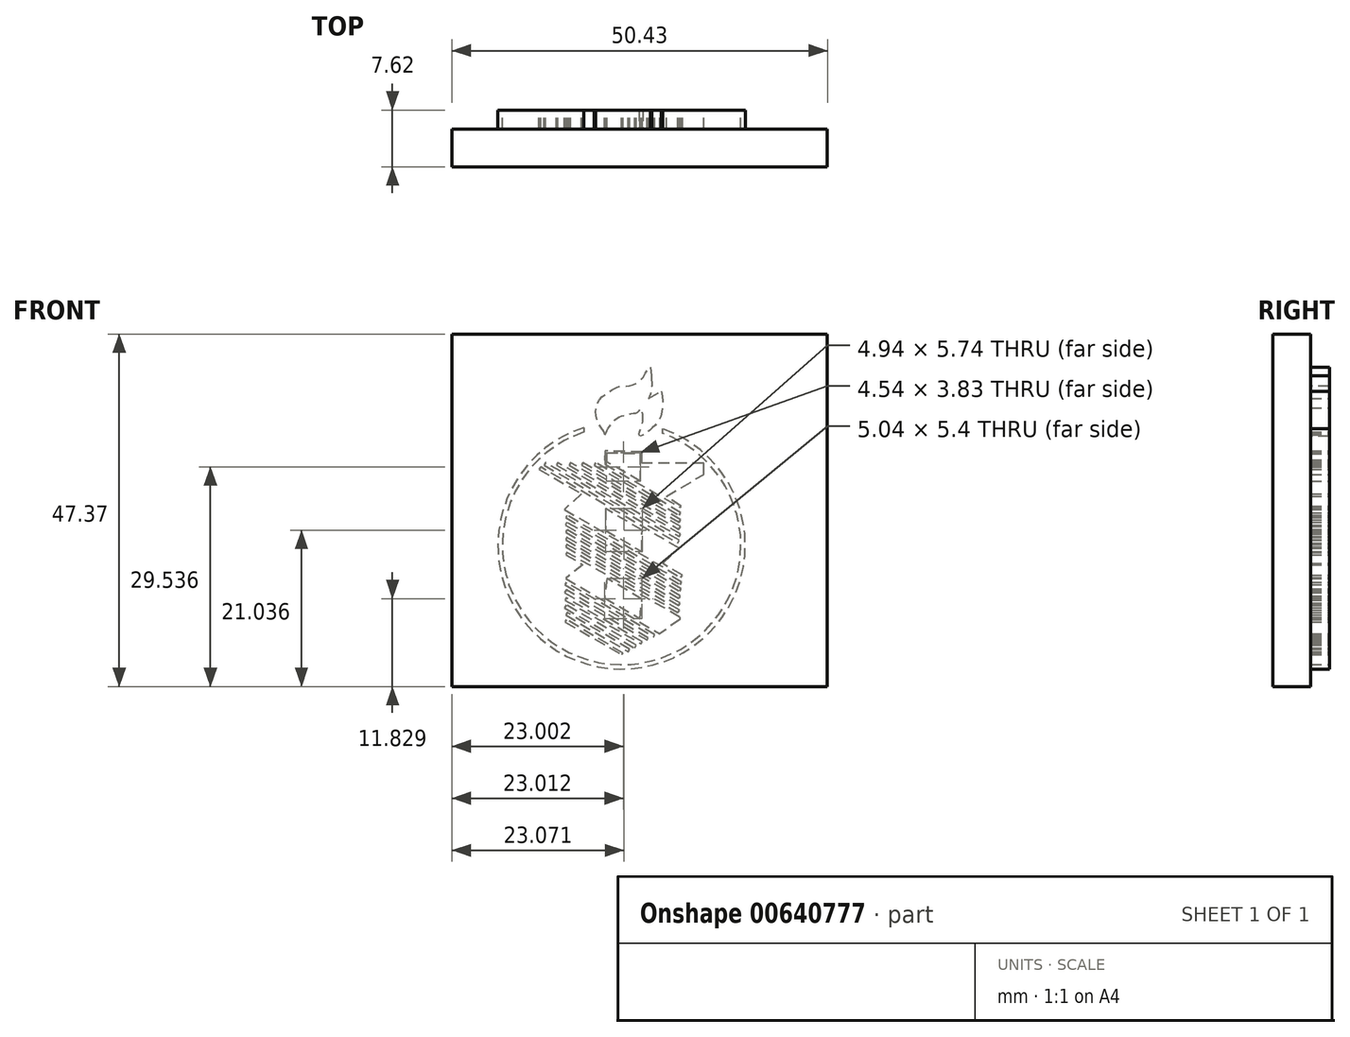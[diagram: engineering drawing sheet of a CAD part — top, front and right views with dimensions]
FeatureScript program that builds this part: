
annotation { "Feature Type Name" : "Feature", "Feature Type Description" : "" }
export const myFeature = defineFeature(function(context is Context, id is Id, definition is map)
    precondition{}
    {
        {
            var Q0;
            Q0=qCreatedBy(makeId("Front.planeOp"),FACE);
            var sketch = newSketch(context, id + "F0", { "sketchPlane" : qUnion([Q0])});
            skArc(sketch, "E0", {"start": v(20.24, 37.87) * mm, "mid": v(25.08, 5.42) * mm, "end": v(30.76, 37.74) * mm});
            skPoint(sketch, "E0.first.point", {"position": v(8.97, 25.16) * mm});
            skPoint(sketch, "E0.second.point", {"position": v(41.48, 18.25) * mm});
            skPoint(sketch, "E0.third.point", {"position": v(33.4, 7.53) * mm});
            skArc(sketch, "E1", {"start": v(20.24, 37.25) * mm, "mid": v(25.08, 6.01) * mm, "end": v(30.76, 37.1) * mm});
            skLineSegment(sketch, "E2", {"start": v(20.24, 37.87) * mm, "end": v(20.24, 37.25) * mm});
            skLineSegment(sketch, "E3", {"start": v(30.76, 37.74) * mm, "end": v(30.76, 37.1) * mm});
            skFitSpline(sketch, "E4", {"points": [v(23.05, 36.92) * mm, v(22.85, 37.48) * mm, v(22.4, 38.11) * mm, v(22.01, 38.86) * mm, v(21.84, 39.64) * mm, v(21.84, 40.27) * mm, v(22.01, 41.04) * mm, v(22.37, 41.63) * mm, v(23.03, 42.32) * mm, v(24.3, 43.12) * mm, v(25.07, 43.44) * mm, v(26.14, 43.44) * mm, v(26.56, 43.54) * mm, v(27.31, 43.8) * mm, v(27.76, 44.12) * mm, v(28.38, 44.9) * mm, v(28.59, 45.41) * mm, v(29.15, 45.99) * mm], "startDerivative": vector(-3, 11.07) * mm, "endDerivative": vector(11.27, 9.68) * mm});
            skLineSegment(sketch, "E5", {"start": v(29.15, 45.99) * mm, "end": v(29.29, 44.84) * mm});
            skFitSpline(sketch, "E6", {"points": [v(29.29, 44.84) * mm, v(29.29, 42.93) * mm, v(28.94, 41.79) * mm], "startDerivative": vector(0.22, -3.65) * mm, "endDerivative": vector(-0.97, -2.41) * mm});
            skLineSegment(sketch, "E7", {"start": v(28.94, 41.79) * mm, "end": v(30.64, 42.74) * mm});
            skFitSpline(sketch, "E8", {"points": [v(30.64, 42.74) * mm, v(30.76, 42.12) * mm, v(30.64, 39.59) * mm, v(29.99, 38.42) * mm, v(28.96, 37.4) * mm, v(27.79, 36.72) * mm, v(27.64, 37.04) * mm, v(28.01, 38.09) * mm, v(28.16, 39.45) * mm, v(28.05, 40.5) * mm], "startDerivative": vector(1.51, -5.83) * mm, "endDerivative": vector(-1.38, 9.53) * mm});
            skFitSpline(sketch, "E9", {"points": [v(23.05, 36.92) * mm, v(23.38, 37.55) * mm, v(23.8, 38.2) * mm, v(24.3, 38.82) * mm, v(24.9, 39.27) * mm, v(25.84, 39.58) * mm, v(26.67, 39.77) * mm, v(27.3, 39.86) * mm, v(27.41, 39.94) * mm, v(27.58, 40.05) * mm, v(27.7, 40.2) * mm, v(28.05, 40.5) * mm], "startDerivative": vector(2.94, 6.1) * mm, "endDerivative": vector(5.03, 3.75) * mm});
            skLineSegment(sketch, "E10", {"start": v(23.26, 33.53) * mm, "end": v(23.26, 34.5) * mm});
            skLineSegment(sketch, "E11", {"start": v(23.26, 34.5) * mm, "end": v(27.8, 34.37) * mm});
            skLineSegment(sketch, "E12", {"start": v(27.8, 34.37) * mm, "end": v(27.8, 30.68) * mm});
            skLineSegment(sketch, "E13", {"start": v(27.8, 30.68) * mm, "end": v(23.26, 33.28) * mm});
            skLineSegment(sketch, "E14", {"start": v(23.05, 33.28) * mm, "end": v(23.05, 32.94) * mm});
            skLineSegment(sketch, "E15", {"start": v(23.05, 32.94) * mm, "end": v(33.19, 27.13) * mm});
            skLineSegment(sketch, "E16", {"start": v(33.19, 27.13) * mm, "end": v(33.3, 27.34) * mm});
            skLineSegment(sketch, "E17", {"start": v(33.3, 27.34) * mm, "end": v(31.33, 28.64) * mm});
            skLineSegment(sketch, "E18", {"start": v(31.33, 28.64) * mm, "end": v(36.34, 31.59) * mm});
            skLineSegment(sketch, "E19", {"start": v(36.34, 31.59) * mm, "end": v(36.34, 33.07) * mm});
            skLineSegment(sketch, "E20", {"start": v(36.34, 33.07) * mm, "end": v(28.05, 33.07) * mm});
            skLineSegment(sketch, "E21", {"start": v(28.05, 33.07) * mm, "end": v(28.05, 34.59) * mm});
            skLineSegment(sketch, "E22", {"start": v(28.05, 34.59) * mm, "end": v(23.05, 34.74) * mm});
            skLineSegment(sketch, "E23", {"start": v(23.05, 34.74) * mm, "end": v(23.02, 33.53) * mm});
            skLineSegment(sketch, "E24", {"start": v(21.8, 33.17) * mm, "end": v(21.62, 32.86) * mm});
            skLineSegment(sketch, "E25", {"start": v(21.62, 32.86) * mm, "end": v(33.06, 26.1) * mm});
            skLineSegment(sketch, "E26", {"start": v(33.06, 26.1) * mm, "end": v(33.26, 26.44) * mm});
            skLineSegment(sketch, "E27", {"start": v(33.26, 26.44) * mm, "end": v(21.8, 33.17) * mm});
            skLineSegment(sketch, "E28", {"start": v(20.1, 33.17) * mm, "end": v(19.9, 32.83) * mm});
            skLineSegment(sketch, "E29", {"start": v(19.9, 32.83) * mm, "end": v(33.02, 25.13) * mm});
            skLineSegment(sketch, "E30", {"start": v(33.02, 25.13) * mm, "end": v(33.23, 25.49) * mm});
            skLineSegment(sketch, "E31", {"start": v(33.23, 25.49) * mm, "end": v(20.1, 33.17) * mm});
            skLineSegment(sketch, "E32", {"start": v(18.44, 33.17) * mm, "end": v(18.24, 32.83) * mm});
            skLineSegment(sketch, "E33", {"start": v(18.24, 32.83) * mm, "end": v(32.98, 24.18) * mm});
            skLineSegment(sketch, "E34", {"start": v(32.98, 24.18) * mm, "end": v(33.21, 24.58) * mm});
            skLineSegment(sketch, "E35", {"start": v(33.21, 24.58) * mm, "end": v(18.44, 33.17) * mm});
            skLineSegment(sketch, "E36", {"start": v(16.75, 33.17) * mm, "end": v(16.55, 32.83) * mm});
            skLineSegment(sketch, "E37", {"start": v(16.55, 32.83) * mm, "end": v(33.02, 23.25) * mm});
            skLineSegment(sketch, "E38", {"start": v(33.02, 23.25) * mm, "end": v(33.21, 23.58) * mm});
            skLineSegment(sketch, "E39", {"start": v(33.21, 23.58) * mm, "end": v(16.75, 33.17) * mm});
            skLineSegment(sketch, "E40", {"start": v(15.08, 33.17) * mm, "end": v(14.88, 32.83) * mm});
            skLineSegment(sketch, "E41", {"start": v(14.88, 32.83) * mm, "end": v(32.84, 22.38) * mm});
            skLineSegment(sketch, "E42", {"start": v(32.84, 22.38) * mm, "end": v(33.02, 22.7) * mm});
            skLineSegment(sketch, "E43", {"start": v(33.02, 22.7) * mm, "end": v(15.08, 33.17) * mm});
            skLineSegment(sketch, "E44", {"start": v(14.41, 32.58) * mm, "end": v(14.21, 32.23) * mm});
            skLineSegment(sketch, "E45", {"start": v(14.21, 32.23) * mm, "end": v(19.9, 28.97) * mm});
            skLineSegment(sketch, "E46", {"start": v(19.9, 28.97) * mm, "end": v(17.61, 26.89) * mm});
            skLineSegment(sketch, "E47", {"start": v(17.61, 26.89) * mm, "end": v(33.24, 17.72) * mm});
            skLineSegment(sketch, "E48", {"start": v(33.24, 17.72) * mm, "end": v(33.47, 18.05) * mm});
            skLineSegment(sketch, "E49", {"start": v(33.47, 18.05) * mm, "end": v(30.81, 19.6) * mm});
            skLineSegment(sketch, "E50", {"start": v(30.81, 19.6) * mm, "end": v(33.02, 21.67) * mm});
            skLineSegment(sketch, "E51", {"start": v(33.02, 21.67) * mm, "end": v(14.41, 32.58) * mm});
            skLineSegment(sketch, "E52", {"start": v(17.96, 26.06) * mm, "end": v(17.79, 25.77) * mm});
            skLineSegment(sketch, "E53", {"start": v(17.79, 25.77) * mm, "end": v(33.18, 16.76) * mm});
            skLineSegment(sketch, "E54", {"start": v(33.18, 16.76) * mm, "end": v(33.37, 17.1) * mm});
            skLineSegment(sketch, "E55", {"start": v(33.37, 17.1) * mm, "end": v(17.96, 26.06) * mm});
            skLineSegment(sketch, "E56", {"start": v(17.96, 25.13) * mm, "end": v(17.76, 24.79) * mm});
            skLineSegment(sketch, "E57", {"start": v(17.76, 24.79) * mm, "end": v(33.13, 15.86) * mm});
            skLineSegment(sketch, "E58", {"start": v(33.13, 15.86) * mm, "end": v(33.32, 16.18) * mm});
            skLineSegment(sketch, "E59", {"start": v(33.32, 16.18) * mm, "end": v(17.96, 25.13) * mm});
            skLineSegment(sketch, "E60", {"start": v(17.96, 24.13) * mm, "end": v(17.78, 23.81) * mm});
            skLineSegment(sketch, "E61", {"start": v(17.78, 23.81) * mm, "end": v(33.02, 14.93) * mm});
            skLineSegment(sketch, "E62", {"start": v(33.02, 14.93) * mm, "end": v(33.2, 15.23) * mm});
            skLineSegment(sketch, "E63", {"start": v(33.2, 15.23) * mm, "end": v(17.96, 24.13) * mm});
            skLineSegment(sketch, "E64", {"start": v(17.96, 23.12) * mm, "end": v(17.78, 22.81) * mm});
            skLineSegment(sketch, "E65", {"start": v(17.78, 22.81) * mm, "end": v(32.95, 14) * mm});
            skLineSegment(sketch, "E66", {"start": v(32.95, 14) * mm, "end": v(33.15, 14.28) * mm});
            skLineSegment(sketch, "E67", {"start": v(33.15, 14.28) * mm, "end": v(17.96, 23.12) * mm});
            skLineSegment(sketch, "E68", {"start": v(17.96, 22.17) * mm, "end": v(17.78, 21.86) * mm});
            skLineSegment(sketch, "E69", {"start": v(17.78, 21.86) * mm, "end": v(32.86, 13.03) * mm});
            skLineSegment(sketch, "E70", {"start": v(32.86, 13.03) * mm, "end": v(33.08, 13.33) * mm});
            skLineSegment(sketch, "E71", {"start": v(33.08, 13.33) * mm, "end": v(17.96, 22.17) * mm});
            skLineSegment(sketch, "E72", {"start": v(17.96, 21.1) * mm, "end": v(17.78, 20.8) * mm});
            skLineSegment(sketch, "E73", {"start": v(17.78, 20.8) * mm, "end": v(20.1, 19.46) * mm});
            skLineSegment(sketch, "E74", {"start": v(20.1, 19.46) * mm, "end": v(17.78, 17.58) * mm});
            skLineSegment(sketch, "E75", {"start": v(17.78, 17.58) * mm, "end": v(30.44, 10.17) * mm});
            skLineSegment(sketch, "E76", {"start": v(33.12, 12.42) * mm, "end": v(17.96, 21.1) * mm});
            skLineSegment(sketch, "E77", {"start": v(23.14, 26.97) * mm, "end": v(23.12, 24.05) * mm});
            skLineSegment(sketch, "E78", {"start": v(23.12, 24.05) * mm, "end": v(28, 21.23) * mm});
            skLineSegment(sketch, "E79", {"start": v(28, 21.23) * mm, "end": v(28.06, 24.08) * mm});
            skLineSegment(sketch, "E80", {"start": v(28.06, 24.08) * mm, "end": v(23.14, 26.97) * mm});
            skLineSegment(sketch, "E81", {"start": v(23.3, 17.6) * mm, "end": v(23, 15) * mm});
            skLineSegment(sketch, "E82", {"start": v(23, 15) * mm, "end": v(27.78, 12.19) * mm});
            skLineSegment(sketch, "E83", {"start": v(27.78, 12.19) * mm, "end": v(28.04, 14.82) * mm});
            skLineSegment(sketch, "E84", {"start": v(28.04, 14.82) * mm, "end": v(23.3, 17.6) * mm});
            skLineSegment(sketch, "E85", {"start": v(17.84, 17.1) * mm, "end": v(17.65, 16.77) * mm});
            skLineSegment(sketch, "E86", {"start": v(17.65, 16.77) * mm, "end": v(29.61, 9.77) * mm});
            skLineSegment(sketch, "E87", {"start": v(29.61, 9.77) * mm, "end": v(29.77, 10.04) * mm});
            skLineSegment(sketch, "E88", {"start": v(29.77, 10.04) * mm, "end": v(17.84, 17.1) * mm});
            skLineSegment(sketch, "E89", {"start": v(17.84, 16.05) * mm, "end": v(17.63, 15.68) * mm});
            skLineSegment(sketch, "E90", {"start": v(17.63, 15.68) * mm, "end": v(28.72, 9.33) * mm});
            skLineSegment(sketch, "E91", {"start": v(28.72, 9.33) * mm, "end": v(28.87, 9.6) * mm});
            skLineSegment(sketch, "E92", {"start": v(28.87, 9.6) * mm, "end": v(17.84, 16.05) * mm});
            skLineSegment(sketch, "E93", {"start": v(17.84, 15) * mm, "end": v(17.66, 14.7) * mm});
            skLineSegment(sketch, "E94", {"start": v(17.66, 14.7) * mm, "end": v(27.92, 8.82) * mm});
            skLineSegment(sketch, "E95", {"start": v(27.92, 8.82) * mm, "end": v(28.06, 9.06) * mm});
            skLineSegment(sketch, "E96", {"start": v(28.06, 9.06) * mm, "end": v(17.84, 15) * mm});
            skLineSegment(sketch, "E97", {"start": v(17.84, 14.05) * mm, "end": v(17.61, 13.65) * mm});
            skLineSegment(sketch, "E98", {"start": v(17.61, 13.65) * mm, "end": v(27.04, 8.25) * mm});
            skLineSegment(sketch, "E99", {"start": v(27.04, 8.25) * mm, "end": v(27.26, 8.62) * mm});
            skLineSegment(sketch, "E100", {"start": v(27.26, 8.62) * mm, "end": v(17.84, 14.05) * mm});
            skLineSegment(sketch, "E101", {"start": v(17.97, 13.02) * mm, "end": v(17.78, 12.68) * mm});
            skLineSegment(sketch, "E102", {"start": v(17.78, 12.68) * mm, "end": v(26.2, 7.74) * mm});
            skLineSegment(sketch, "E103", {"start": v(26.2, 7.74) * mm, "end": v(26.39, 8.08) * mm});
            skLineSegment(sketch, "E104", {"start": v(26.39, 8.08) * mm, "end": v(17.97, 13.02) * mm});
            skLineSegment(sketch, "E105", {"start": v(17.88, 12.07) * mm, "end": v(17.69, 11.72) * mm});
            skLineSegment(sketch, "E106", {"start": v(17.69, 11.72) * mm, "end": v(25.28, 7.38) * mm});
            skLineSegment(sketch, "E107", {"start": v(25.28, 7.38) * mm, "end": v(25.47, 7.58) * mm});
            skLineSegment(sketch, "E108", {"start": v(25.47, 7.58) * mm, "end": v(17.88, 12.07) * mm});
            skLineSegment(sketch, "E109", {"start": v(33.12, 12.42) * mm, "end": v(33.12, 12.09) * mm});
            skLineSegment(sketch, "E110", {"start": v(33.12, 12.09) * mm, "end": v(30.44, 10.17) * mm});
            skLineSegment(sketch, "E111", {"start": v(23.02, 33.53) * mm, "end": v(23.05, 33.28) * mm});
            skLineSegment(sketch, "E112", {"start": v(23.26, 33.53) * mm, "end": v(23.26, 33.28) * mm});
            skSolve(sketch);
        }
        {
            var Q0;
            Q0=makeQuery(id+"F0.imprint","IMPRINT",FACE,{"disambiguationData":[TD([[makeQuery(id+"F0.imprint","IMPRINT",EDGE,{"derivedFrom":sQuery(id+"F0.wireOp",EDGE,"E0")}),1.0]])]});
            var Q1;
            Q1=makeQuery(id+"F0.imprint","IMPRINT",FACE,{"disambiguationData":[TD([[makeQuery(id+"F0.imprint","IMPRINT",EDGE,{"derivedFrom":sQuery(id+"F0.wireOp",EDGE,"E4")}),-1.0]])]});
            var Q2;
            Q2=makeQuery(id+"F0.imprint","IMPRINT",FACE,{"disambiguationData":[TD([[makeQuery(id+"F0.imprint","IMPRINT",EDGE,{"derivedFrom":sQuery(id+"F0.wireOp",EDGE,"y2vc7ffB-SEBn-57zv-CqBY-3sHhlxAjugWr")}),1.0]])]});
            var Q3;
            Q3=makeQuery(id+"F0.imprint","IMPRINT",FACE,{"disambiguationData":[TD([[makeQuery(id+"F0.imprint","IMPRINT",EDGE,{"derivedFrom":sQuery(id+"F0.wireOp",EDGE,"E24")}),1.0]])]});
            var Q4;
            Q4=makeQuery(id+"F0.imprint","IMPRINT",FACE,{"disambiguationData":[TD([[makeQuery(id+"F0.imprint","IMPRINT",EDGE,{"derivedFrom":sQuery(id+"F0.wireOp",EDGE,"E28")}),1.0]])]});
            var Q5;
            Q5=makeQuery(id+"F0.imprint","IMPRINT",FACE,{"disambiguationData":[TD([[makeQuery(id+"F0.imprint","IMPRINT",EDGE,{"derivedFrom":sQuery(id+"F0.wireOp",EDGE,"E32")}),1.0]])]});
            var Q6;
            Q6=makeQuery(id+"F0.imprint","IMPRINT",FACE,{"disambiguationData":[TD([[makeQuery(id+"F0.imprint","IMPRINT",EDGE,{"derivedFrom":sQuery(id+"F0.wireOp",EDGE,"E36")}),1.0]])]});
            var Q7;
            Q7=makeQuery(id+"F0.imprint","IMPRINT",FACE,{"disambiguationData":[TD([[makeQuery(id+"F0.imprint","IMPRINT",EDGE,{"derivedFrom":sQuery(id+"F0.wireOp",EDGE,"E40")}),1.0]])]});
            var Q8;
            Q8=makeQuery(id+"F0.imprint","IMPRINT",FACE,{"disambiguationData":[TD([[makeQuery(id+"F0.imprint","IMPRINT",EDGE,{"derivedFrom":sQuery(id+"F0.wireOp",EDGE,"E52")}),1.0]])]});
            var Q9;
            Q9=makeQuery(id+"F0.imprint","IMPRINT",FACE,{"disambiguationData":[TD([[makeQuery(id+"F0.imprint","IMPRINT",EDGE,{"derivedFrom":sQuery(id+"F0.wireOp",EDGE,"E56")}),1.0]])]});
            var Q10;
            Q10=makeQuery(id+"F0.imprint","IMPRINT",FACE,{"disambiguationData":[TD([[makeQuery(id+"F0.imprint","IMPRINT",EDGE,{"derivedFrom":sQuery(id+"F0.wireOp",EDGE,"E60")}),1.0]])]});
            var Q11;
            Q11=makeQuery(id+"F0.imprint","IMPRINT",FACE,{"disambiguationData":[TD([[makeQuery(id+"F0.imprint","IMPRINT",EDGE,{"derivedFrom":sQuery(id+"F0.wireOp",EDGE,"E64")}),1.0]])]});
            var Q12;
            Q12=makeQuery(id+"F0.imprint","IMPRINT",FACE,{"disambiguationData":[TD([[makeQuery(id+"F0.imprint","IMPRINT",EDGE,{"derivedFrom":sQuery(id+"F0.wireOp",EDGE,"E68")}),1.0]])]});
            var Q13;
            Q13=makeQuery(id+"F0.imprint","IMPRINT",FACE,{"disambiguationData":[TD([[makeQuery(id+"F0.imprint","IMPRINT",EDGE,{"derivedFrom":sQuery(id+"F0.wireOp",EDGE,"E85")}),1.0]])]});
            var Q14;
            Q14=makeQuery(id+"F0.imprint","IMPRINT",FACE,{"disambiguationData":[TD([[makeQuery(id+"F0.imprint","IMPRINT",EDGE,{"derivedFrom":sQuery(id+"F0.wireOp",EDGE,"E89")}),1.0]])]});
            var Q15;
            Q15=makeQuery(id+"F0.imprint","IMPRINT",FACE,{"disambiguationData":[TD([[makeQuery(id+"F0.imprint","IMPRINT",EDGE,{"derivedFrom":sQuery(id+"F0.wireOp",EDGE,"E93")}),1.0]])]});
            var Q16;
            Q16=makeQuery(id+"F0.imprint","IMPRINT",FACE,{"disambiguationData":[TD([[makeQuery(id+"F0.imprint","IMPRINT",EDGE,{"derivedFrom":sQuery(id+"F0.wireOp",EDGE,"E97")}),1.0]])]});
            var Q17;
            Q17=makeQuery(id+"F0.imprint","IMPRINT",FACE,{"disambiguationData":[TD([[makeQuery(id+"F0.imprint","IMPRINT",EDGE,{"derivedFrom":sQuery(id+"F0.wireOp",EDGE,"E101")}),1.0]])]});
            var Q18;
            Q18=makeQuery(id+"F0.imprint","IMPRINT",FACE,{"disambiguationData":[TD([[makeQuery(id+"F0.imprint","IMPRINT",EDGE,{"derivedFrom":sQuery(id+"F0.wireOp",EDGE,"E105")}),1.0]])]});
            var Q19;
            Q19=makeQuery(id+"F0.imprint","IMPRINT",FACE,{"disambiguationData":[TD([[makeQuery(id+"F0.imprint","IMPRINT",EDGE,{"derivedFrom":sQuery(id+"F0.wireOp",EDGE,"E72")}),1.0]])]});
            var Q20;
            Q20=makeQuery(id+"F0.imprint","IMPRINT",FACE,{"disambiguationData":[TD([[makeQuery(id+"F0.imprint","IMPRINT",EDGE,{"derivedFrom":sQuery(id+"F0.wireOp",EDGE,"E44")}),1.0]])]});
            var Q21;
            Q21=makeQuery(id+"F0.imprint","IMPRINT",FACE,{"disambiguationData":[TD([[makeQuery(id+"F0.imprint","IMPRINT",EDGE,{"derivedFrom":sQuery(id+"F0.wireOp",EDGE,"E10")}),1.0]])]});
            extrude(context, id + "F1", {"entities" : qUnion([Q0, Q1, Q2, Q3, Q4, Q5, Q6, Q7, Q8, Q9, Q10, Q11, Q12, Q13, Q14, Q15, Q16, Q17, Q18, Q19, Q20, Q21]), "depth" : 2.54 * mm, "offsetDistance" : 25.4 * mm});
        }
        {
            var Q0;
            Q0=makeQuery(id+"F1.opExtrude","CAP_FACE",FACE,{"disambiguationData":[OSD([sQuery(id+"F0.wireOp",EDGE,"E44"),sQuery(id+"F0.wireOp",EDGE,"E45"),sQuery(id+"F0.wireOp",EDGE,"E46"),sQuery(id+"F0.wireOp",EDGE,"E47"),sQuery(id+"F0.wireOp",EDGE,"E48"),sQuery(id+"F0.wireOp",EDGE,"E49"),sQuery(id+"F0.wireOp",EDGE,"E50"),sQuery(id+"F0.wireOp",EDGE,"E51"),sQuery(id+"F0.wireOp",EDGE,"E77"),sQuery(id+"F0.wireOp",EDGE,"E78"),sQuery(id+"F0.wireOp",EDGE,"E79"),sQuery(id+"F0.wireOp",EDGE,"E80")])],"isStart":false});
            var sketch = newSketch(context, id + "F2", { "sketchPlane" : qUnion([Q0])});
            skLineSegment(sketch, "E113.bottom", {"start": v(2.52, 50.43) * mm, "end": v(52.95, 50.43) * mm});
            skLineSegment(sketch, "E113.top", {"start": v(2.52, 3.06) * mm, "end": v(52.95, 3.06) * mm});
            skLineSegment(sketch, "E113.left", {"start": v(2.52, 50.43) * mm, "end": v(2.52, 3.06) * mm});
            skLineSegment(sketch, "E113.right", {"start": v(52.95, 50.43) * mm, "end": v(52.95, 3.06) * mm});
            skSolve(sketch);
        }
        {
            var Q0;
            Q0 = qSketchRegion(id + "F2", true);
            extrude(context, id + "F3", {"entities" : qUnion([Q0]), "depth" : 5.08 * mm, "offsetDistance" : 25.4 * mm});
        }
    });
